# Revit family: Lighting-Luminii-Stenos_Trimmed_Linear_Downlight_Wallwash
name_source: partatom
category: Lighting Fixtures
units: mm (PartAtom-declared; Revit-internal decimal feet)

## family parameters
Cut with Voids When Loaded = No
Host = Face
Light Source = Yes
OmniClass Number = 23.80.70.11.14.21
OmniClass Title = Spots and Tracklight Specialties
Part Type = Normal
Room Calculation Point = No
Round Connector Dimension = Use Diameter
Shared = Yes

## types (3) — shared parameters
Apparent Load = 3 VA
Assembly Code = D5040.50
C End Caps Width = 0.47 "
CCT = 2700
Color Filter = 16777215
Current Amps = 50 A
Depth = 1.95 "
Description = Track System
Dimming Lamp Color Temperature Shift = <None>
Environment = Indoor
Finish = Metal - Luminii - Silver Anodized Aluminum
Frequency = 60 Hz
Has Battery Backup = No
Has Dimming = Yes
Housing Protection Rating = IP20 Dry/IP66 Wet Series
Initial Color Comments = Perfomance based on 3500K Photometric Web File
Keynote = 26 50 00
Lamp = LED
Lamp Life = 1
Lens Material = Plastic - Luminii - Frosted Lens
Load Classification = Lighting
Manufacturer = Luminii
Mounting Method = Surface Mount
Number of Poles = 1
Operating Temperature = Consult Manufacturer for more Information
Phase = 1
Power Factor = 1
Power Source Type = Driver
Product Page URL = https://www.luminii.com
Tilt Angle = 90.00°
URL = https://www.luminii.com
Version = 2020 - v1.0a
Voltage = 120 V
Voltage Comments = 120VAC - 277VAC
Warranty URL = https://www.luminii.com
Width = 1.06 "
zero-valued in all types: Default Elevation

## per-type parameters (varying)
| type | C Right Support | Constraints | Lumen Output | Model | Photometric Web File | Wattage Comments |
| Track Module - 3" | No | 1 | 250 lm | SD-3 | generic.ies | 2.6 W |
| Track Module - 5" | Yes | 2 | 520 lm | SD-5 | generic.ies | 5.4 W |
| Track Module - 12" | Yes | 3 | 1260 lm | SD-12 | SD-5-30K-SO-WW-BK.IES | 13.0 W |

## geometry (parser evidence)
native form markers: Sweep x12
no freeform markers — native parametric forms only
